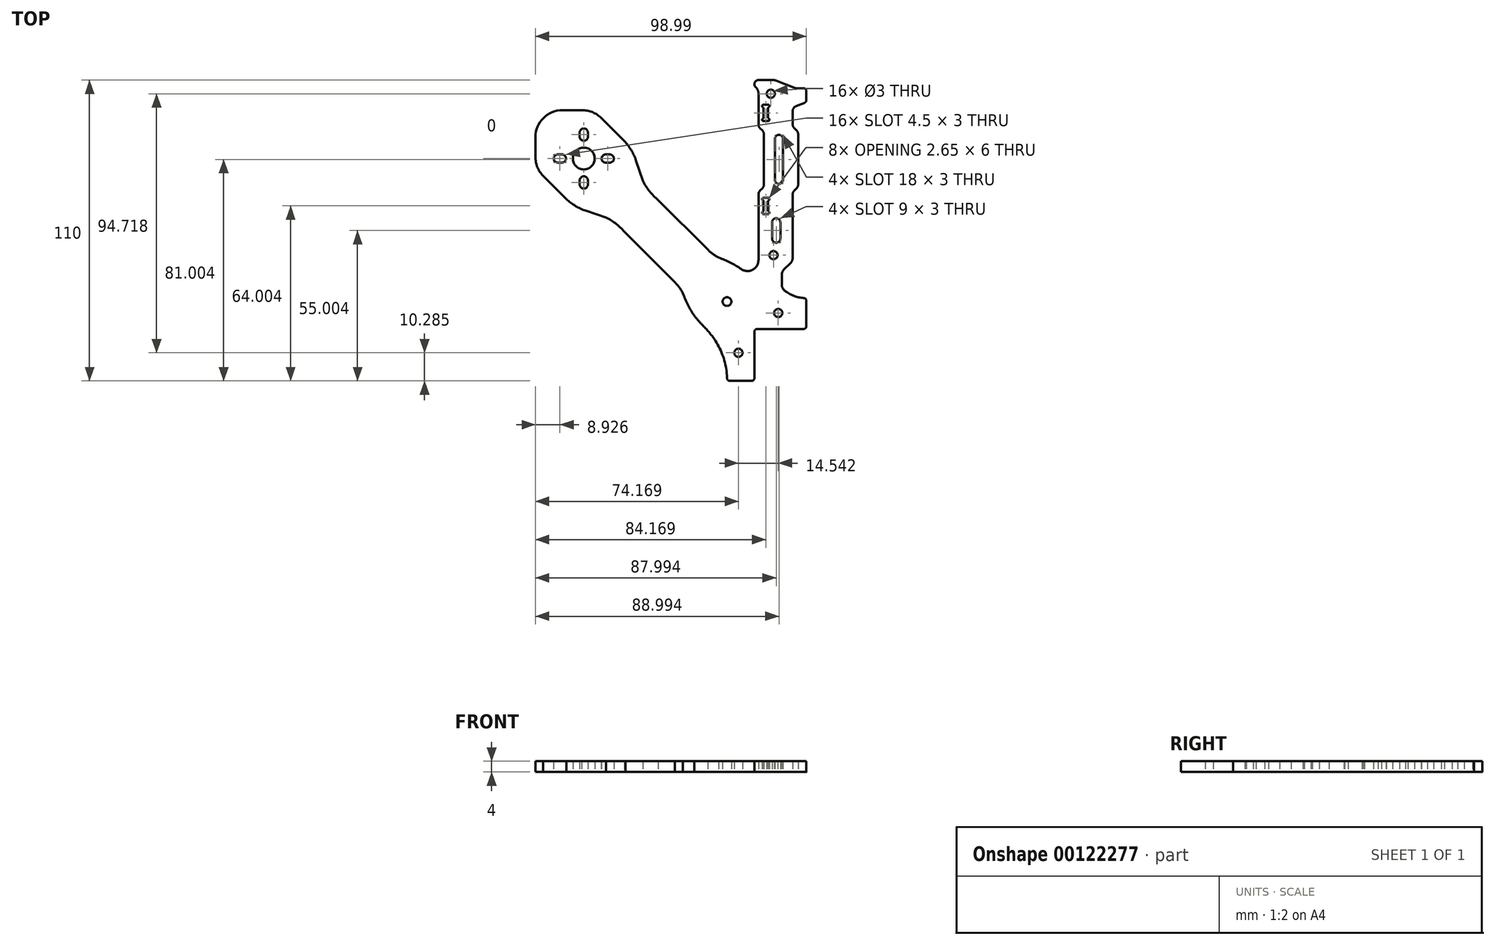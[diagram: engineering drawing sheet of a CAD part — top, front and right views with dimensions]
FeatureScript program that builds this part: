
annotation { "Feature Type Name" : "Feature", "Feature Type Description" : "" }
export const myFeature = defineFeature(function(context is Context, id is Id, definition is map)
    precondition{}
    {
        {
            var Q0;
            Q0=qCreatedBy(makeId("Top.planeOp"),FACE);
            var sketch = newSketch(context, id + "F0", { "sketchPlane" : qUnion([Q0])});
            skLineSegment(sketch, "E0", {"start": v(-69.83, -19.02) * mm, "end": v(-75.26, -19.02) * mm});
            skArc(sketch, "E1", {"start": v(-75.26, -19.02) * mm, "mid": v(-76.66, -19.98) * mm, "end": v(-76.26, -21.63) * mm});
            skLineSegment(sketch, "E2", {"start": v(-62.3, -21.8) * mm, "end": v(-68.72, -19.23) * mm});
            skArc(sketch, "E3", {"start": v(-75.26, -23.87) * mm, "mid": v(-75.52, -22.65) * mm, "end": v(-76.26, -21.63) * mm});
            skArc(sketch, "E4", {"start": v(-68.72, -19.23) * mm, "mid": v(-69.27, -19.07) * mm, "end": v(-69.83, -19.02) * mm});
            skArc(sketch, "E5", {"start": v(-62.3, -21.8) * mm, "mid": v(-61.75, -21.96) * mm, "end": v(-61.18, -22.02) * mm});
            skLineSegment(sketch, "E6", {"start": v(-61.18, -22.02) * mm, "end": v(-58.76, -22.02) * mm});
            skArc(sketch, "E7", {"start": v(-57.76, -23.02) * mm, "mid": v(-58.05, -22.3) * mm, "end": v(-58.76, -22.02) * mm});
            skLineSegment(sketch, "E8", {"start": v(-73.26, -57.19) * mm, "end": v(-73.26, -38.84) * mm});
            skLineSegment(sketch, "E9", {"start": v(-73.84, -37.43) * mm, "end": v(-74.67, -36.6) * mm});
            skLineSegment(sketch, "E10", {"start": v(-74.67, -59.43) * mm, "end": v(-73.84, -58.6) * mm});
            skLineSegment(sketch, "E11", {"start": v(-75.26, -23.87) * mm, "end": v(-75.26, -35.19) * mm});
            skArc(sketch, "E12", {"start": v(-75.26, -35.19) * mm, "mid": v(-75.1, -35.95) * mm, "end": v(-74.67, -36.6) * mm});
            skArc(sketch, "E13", {"start": v(-73.26, -38.84) * mm, "mid": v(-73.4, -38.08) * mm, "end": v(-73.84, -37.43) * mm});
            skArc(sketch, "E14", {"start": v(-74.67, -59.43) * mm, "mid": v(-75.1, -60.08) * mm, "end": v(-75.26, -60.84) * mm});
            skArc(sketch, "E15", {"start": v(-73.84, -58.6) * mm, "mid": v(-73.4, -57.95) * mm, "end": v(-73.26, -57.19) * mm});
            skCircle(sketch, "E16", {"center": v(-139.07, -47.7) * mm, "radius": 4 * mm});
            skArc(sketch, "E17", {"start": v(-148.57, -46.2) * mm, "mid": v(-150.07, -47.7) * mm, "end": v(-148.57, -49.2) * mm});
            skArc(sketch, "E18", {"start": v(-147.07, -49.2) * mm, "mid": v(-145.57, -47.7) * mm, "end": v(-147.07, -46.2) * mm});
            skArc(sketch, "E19", {"start": v(-137.57, -38.2) * mm, "mid": v(-139.07, -36.7) * mm, "end": v(-140.57, -38.2) * mm});
            skArc(sketch, "E20", {"start": v(-140.57, -39.7) * mm, "mid": v(-139.07, -41.2) * mm, "end": v(-137.57, -39.7) * mm});
            skArc(sketch, "E21", {"start": v(-131.07, -46.2) * mm, "mid": v(-132.57, -47.7) * mm, "end": v(-131.07, -49.2) * mm});
            skArc(sketch, "E22", {"start": v(-129.57, -49.2) * mm, "mid": v(-128.07, -47.7) * mm, "end": v(-129.57, -46.2) * mm});
            skArc(sketch, "E23", {"start": v(-137.57, -55.7) * mm, "mid": v(-139.07, -54.2) * mm, "end": v(-140.57, -55.7) * mm});
            skArc(sketch, "E24", {"start": v(-140.57, -57.2) * mm, "mid": v(-139.07, -58.7) * mm, "end": v(-137.57, -57.2) * mm});
            skLineSegment(sketch, "E25", {"start": v(-148.57, -46.2) * mm, "end": v(-147.07, -46.2) * mm});
            skLineSegment(sketch, "E26", {"start": v(-147.07, -49.2) * mm, "end": v(-148.57, -49.2) * mm});
            skLineSegment(sketch, "E27", {"start": v(-140.57, -38.2) * mm, "end": v(-140.57, -39.7) * mm});
            skLineSegment(sketch, "E28", {"start": v(-137.57, -38.2) * mm, "end": v(-137.57, -39.7) * mm});
            skLineSegment(sketch, "E29", {"start": v(-129.57, -46.2) * mm, "end": v(-131.07, -46.2) * mm});
            skLineSegment(sketch, "E30", {"start": v(-129.57, -49.2) * mm, "end": v(-131.07, -49.2) * mm});
            skLineSegment(sketch, "E31", {"start": v(-137.57, -55.7) * mm, "end": v(-137.57, -57.2) * mm});
            skLineSegment(sketch, "E32", {"start": v(-140.57, -55.7) * mm, "end": v(-140.57, -57.2) * mm});
            skLineSegment(sketch, "E33", {"start": v(-124.22, -41.34) * mm, "end": v(-132.7, -32.85) * mm});
            skLineSegment(sketch, "E34", {"start": v(-153.92, -54.06) * mm, "end": v(-145.44, -62.55) * mm});
            skArc(sketch, "E35", {"start": v(-146.85, -30.02) * mm, "mid": v(-153.85, -32.92) * mm, "end": v(-156.75, -39.92) * mm});
            skLineSegment(sketch, "E36", {"start": v(-146.85, -30.02) * mm, "end": v(-139.78, -30.02) * mm});
            skLineSegment(sketch, "E37", {"start": v(-156.75, -39.92) * mm, "end": v(-156.75, -47) * mm});
            skLineSegment(sketch, "E38", {"start": v(-117.5, -55.83) * mm, "end": v(-119.98, -48.4) * mm});
            skLineSegment(sketch, "E39", {"start": v(-130.94, -69.27) * mm, "end": v(-138.37, -66.8) * mm});
            skArc(sketch, "E40", {"start": v(-123.87, -74.92) * mm, "mid": v(-127.1, -71.72) * mm, "end": v(-130.94, -69.27) * mm});
            skArc(sketch, "E41", {"start": v(-117.5, -55.83) * mm, "mid": v(-115.05, -59.66) * mm, "end": v(-111.85, -62.9) * mm});
            skArc(sketch, "E42", {"start": v(-119.98, -48.4) * mm, "mid": v(-121.73, -44.65) * mm, "end": v(-124.22, -41.34) * mm});
            skArc(sketch, "E43", {"start": v(-145.44, -62.55) * mm, "mid": v(-142.12, -65.04) * mm, "end": v(-138.37, -66.8) * mm});
            skArc(sketch, "E44", {"start": v(-132.7, -32.85) * mm, "mid": v(-135.96, -30.73) * mm, "end": v(-139.78, -30.02) * mm});
            skArc(sketch, "E45", {"start": v(-156.75, -47) * mm, "mid": v(-156.04, -50.8) * mm, "end": v(-153.92, -54.06) * mm});
            skCircle(sketch, "E46", {"center": v(-69.76, -83.02) * mm, "radius": 1.5 * mm});
            skLineSegment(sketch, "E47", {"start": v(-71.76, -28.02) * mm, "end": v(-73.4, -28.02) * mm});
            skLineSegment(sketch, "E48", {"start": v(-71.76, -62.02) * mm, "end": v(-73.4, -62.02) * mm});
            skLineSegment(sketch, "E49", {"start": v(-73.4, -34.02) * mm, "end": v(-71.76, -34.02) * mm});
            skLineSegment(sketch, "E50", {"start": v(-73.4, -68.02) * mm, "end": v(-71.76, -68.02) * mm});
            skArc(sketch, "E51", {"start": v(-73.4, -28.02) * mm, "mid": v(-73.89, -28.39) * mm, "end": v(-73.66, -28.95) * mm});
            skArc(sketch, "E52", {"start": v(-73.66, -33.08) * mm, "mid": v(-73.89, -33.65) * mm, "end": v(-73.4, -34.02) * mm});
            skArc(sketch, "E53", {"start": v(-71.76, -34.02) * mm, "mid": v(-71.27, -33.65) * mm, "end": v(-71.5, -33.08) * mm});
            skArc(sketch, "E54", {"start": v(-71.5, -28.95) * mm, "mid": v(-71.27, -28.39) * mm, "end": v(-71.76, -28.02) * mm});
            skArc(sketch, "E55", {"start": v(-71.5, -62.95) * mm, "mid": v(-71.27, -62.39) * mm, "end": v(-71.76, -62.02) * mm});
            skArc(sketch, "E56", {"start": v(-73.4, -62.02) * mm, "mid": v(-73.89, -62.39) * mm, "end": v(-73.66, -62.95) * mm});
            skArc(sketch, "E57", {"start": v(-73.66, -67.08) * mm, "mid": v(-73.89, -67.65) * mm, "end": v(-73.4, -68.02) * mm});
            skArc(sketch, "E58", {"start": v(-71.76, -68.02) * mm, "mid": v(-71.27, -67.65) * mm, "end": v(-71.5, -67.08) * mm});
            skLineSegment(sketch, "E59", {"start": v(-73.4, -29.38) * mm, "end": v(-73.4, -32.65) * mm});
            skLineSegment(sketch, "E60", {"start": v(-71.76, -32.65) * mm, "end": v(-71.76, -29.38) * mm});
            skLineSegment(sketch, "E61", {"start": v(-71.76, -63.38) * mm, "end": v(-71.76, -66.65) * mm});
            skLineSegment(sketch, "E62", {"start": v(-73.4, -66.65) * mm, "end": v(-73.4, -63.38) * mm});
            skArc(sketch, "E63", {"start": v(-73.4, -29.38) * mm, "mid": v(-73.47, -29.13) * mm, "end": v(-73.66, -28.95) * mm});
            skArc(sketch, "E64", {"start": v(-71.5, -28.95) * mm, "mid": v(-71.69, -29.13) * mm, "end": v(-71.76, -29.38) * mm});
            skArc(sketch, "E65", {"start": v(-71.76, -32.65) * mm, "mid": v(-71.69, -32.9) * mm, "end": v(-71.5, -33.08) * mm});
            skArc(sketch, "E66", {"start": v(-73.66, -33.08) * mm, "mid": v(-73.47, -32.9) * mm, "end": v(-73.4, -32.65) * mm});
            skArc(sketch, "E67", {"start": v(-71.76, -66.65) * mm, "mid": v(-71.69, -66.9) * mm, "end": v(-71.5, -67.08) * mm});
            skArc(sketch, "E68", {"start": v(-73.66, -67.08) * mm, "mid": v(-73.47, -66.9) * mm, "end": v(-73.4, -66.65) * mm});
            skArc(sketch, "E69", {"start": v(-73.4, -63.38) * mm, "mid": v(-73.47, -63.13) * mm, "end": v(-73.66, -62.95) * mm});
            skArc(sketch, "E70", {"start": v(-71.5, -62.95) * mm, "mid": v(-71.69, -63.13) * mm, "end": v(-71.76, -63.38) * mm});
            skLineSegment(sketch, "E71", {"start": v(-75.26, -60.84) * mm, "end": v(-75.26, -84.84) * mm});
            skArc(sketch, "E72", {"start": v(-102.83, -97.02) * mm, "mid": v(-104.16, -94.86) * mm, "end": v(-105.84, -92.95) * mm});
            skArc(sketch, "E73", {"start": v(-93.76, -81.02) * mm, "mid": v(-91.88, -82.65) * mm, "end": v(-89.75, -83.94) * mm});
            skLineSegment(sketch, "E74", {"start": v(-60.76, -38.84) * mm, "end": v(-60.76, -57.19) * mm});
            skLineSegment(sketch, "E75", {"start": v(-62.17, -36.6) * mm, "end": v(-61.34, -37.43) * mm});
            skLineSegment(sketch, "E76", {"start": v(-61.34, -58.6) * mm, "end": v(-62.17, -59.43) * mm});
            skLineSegment(sketch, "E77", {"start": v(-62.76, -83.98) * mm, "end": v(-62.76, -60.84) * mm});
            skArc(sketch, "E78", {"start": v(-62.76, -35.19) * mm, "mid": v(-62.6, -35.95) * mm, "end": v(-62.17, -36.6) * mm});
            skArc(sketch, "E79", {"start": v(-60.76, -38.84) * mm, "mid": v(-60.9, -38.08) * mm, "end": v(-61.34, -37.43) * mm});
            skArc(sketch, "E80", {"start": v(-61.34, -58.6) * mm, "mid": v(-60.9, -57.95) * mm, "end": v(-60.76, -57.19) * mm});
            skArc(sketch, "E81", {"start": v(-62.17, -59.43) * mm, "mid": v(-62.6, -60.08) * mm, "end": v(-62.76, -60.84) * mm});
            skLineSegment(sketch, "E82", {"start": v(-62.76, -30.37) * mm, "end": v(-62.76, -35.19) * mm});
            skLineSegment(sketch, "E83", {"start": v(-66.26, -55.52) * mm, "end": v(-66.26, -40.52) * mm});
            skLineSegment(sketch, "E84", {"start": v(-69.26, -40.52) * mm, "end": v(-69.26, -55.52) * mm});
            skArc(sketch, "E85", {"start": v(-66.26, -40.52) * mm, "mid": v(-67.76, -39.02) * mm, "end": v(-69.26, -40.52) * mm});
            skArc(sketch, "E86", {"start": v(-69.26, -55.52) * mm, "mid": v(-67.76, -57.02) * mm, "end": v(-66.26, -55.52) * mm});
            skLineSegment(sketch, "E87", {"start": v(-67.26, -77.02) * mm, "end": v(-67.26, -71.02) * mm});
            skLineSegment(sketch, "E88", {"start": v(-70.26, -71.02) * mm, "end": v(-70.26, -77.02) * mm});
            skArc(sketch, "E89", {"start": v(-67.26, -71.02) * mm, "mid": v(-68.76, -69.52) * mm, "end": v(-70.26, -71.02) * mm});
            skArc(sketch, "E90", {"start": v(-70.26, -77.02) * mm, "mid": v(-68.76, -78.52) * mm, "end": v(-67.26, -77.02) * mm});
            skCircle(sketch, "E91", {"center": v(-82.58, -118.73) * mm, "radius": 1.5 * mm});
            skCircle(sketch, "E92", {"center": v(-68.04, -104.2) * mm, "radius": 1.5 * mm});
            skLineSegment(sketch, "E93", {"start": v(-58.5, -27.31) * mm, "end": v(-61.5, -28.51) * mm});
            skArc(sketch, "E94", {"start": v(-61.5, -28.51) * mm, "mid": v(-62.41, -29.25) * mm, "end": v(-62.76, -30.37) * mm});
            skLineSegment(sketch, "E95", {"start": v(-57.76, -23.02) * mm, "end": v(-57.76, -26.34) * mm});
            skArc(sketch, "E96", {"start": v(-58.42, -27.28) * mm, "mid": v(-58.46, -27.3) * mm, "end": v(-58.5, -27.31) * mm});
            skArc(sketch, "E97", {"start": v(-58.42, -27.28) * mm, "mid": v(-57.94, -26.92) * mm, "end": v(-57.76, -26.34) * mm});
            skLineSegment(sketch, "E98", {"start": v(-123.87, -74.92) * mm, "end": v(-105.84, -92.95) * mm});
            skLineSegment(sketch, "E99", {"start": v(-93.76, -81.02) * mm, "end": v(-111.85, -62.9) * mm});
            skArc(sketch, "E100", {"start": v(-75.76, -110.02) * mm, "mid": v(-76.46, -110.3) * mm, "end": v(-76.76, -111.02) * mm});
            skLineSegment(sketch, "E101", {"start": v(-75.76, -110.02) * mm, "end": v(-58.76, -110.02) * mm});
            skArc(sketch, "E102", {"start": v(-58.76, -110.02) * mm, "mid": v(-58.05, -109.72) * mm, "end": v(-57.76, -109.02) * mm});
            skLineSegment(sketch, "E103", {"start": v(-76.76, -111.02) * mm, "end": v(-76.76, -128.02) * mm});
            skArc(sketch, "E104", {"start": v(-77.76, -129.02) * mm, "mid": v(-77.05, -128.72) * mm, "end": v(-76.76, -128.02) * mm});
            skCircle(sketch, "E105", {"center": v(-70.76, -24.02) * mm, "radius": 1.5 * mm});
            skCircle(sketch, "E106", {"center": v(-86.76, -100.02) * mm, "radius": 1.6 * mm});
            skArc(sketch, "E107", {"start": v(-98.64, -105.25) * mm, "mid": v(-97.14, -107.06) * mm, "end": v(-95.52, -108.78) * mm});
            skArc(sketch, "E108", {"start": v(-90.99, -114.37) * mm, "mid": v(-93.1, -111.46) * mm, "end": v(-95.52, -108.78) * mm});
            skArc(sketch, "E109", {"start": v(-86.86, -126.19) * mm, "mid": v(-88.2, -120.03) * mm, "end": v(-90.99, -114.37) * mm});
            skArc(sketch, "E110", {"start": v(-81.52, -88.13) * mm, "mid": v(-85.5, -85.77) * mm, "end": v(-89.75, -83.94) * mm});
            skArc(sketch, "E111", {"start": v(-102.83, -97.02) * mm, "mid": v(-101, -101.27) * mm, "end": v(-98.64, -105.25) * mm});
            skArc(sketch, "E112", {"start": v(-81.52, -88.13) * mm, "mid": v(-77.4, -88.38) * mm, "end": v(-75.26, -84.84) * mm});
            skArc(sketch, "E113", {"start": v(-86.74, -128.05) * mm, "mid": v(-86.78, -127.12) * mm, "end": v(-86.86, -126.19) * mm});
            skArc(sketch, "E114", {"start": v(-86.74, -128.05) * mm, "mid": v(-86.44, -128.73) * mm, "end": v(-85.74, -129.02) * mm});
            skLineSegment(sketch, "E115", {"start": v(-85.74, -129.02) * mm, "end": v(-77.76, -129.02) * mm});
            skLineSegment(sketch, "E116", {"start": v(-66.76, -90.32) * mm, "end": v(-66.76, -93.67) * mm});
            skLineSegment(sketch, "E117", {"start": v(-63.7, -86.17) * mm, "end": v(-65.8, -88.13) * mm});
            skArc(sketch, "E118", {"start": v(-65.6, -96.04) * mm, "mid": v(-62.34, -97.89) * mm, "end": v(-58.68, -98.71) * mm});
            skArc(sketch, "E119", {"start": v(-57.76, -99.7) * mm, "mid": v(-58.02, -99.03) * mm, "end": v(-58.68, -98.71) * mm});
            skLineSegment(sketch, "E120", {"start": v(-57.76, -99.7) * mm, "end": v(-57.76, -109.02) * mm});
            skArc(sketch, "E121", {"start": v(-63.7, -86.17) * mm, "mid": v(-63, -85.18) * mm, "end": v(-62.76, -83.98) * mm});
            skArc(sketch, "E122", {"start": v(-65.8, -88.13) * mm, "mid": v(-66.5, -89.12) * mm, "end": v(-66.76, -90.32) * mm});
            skArc(sketch, "E123", {"start": v(-66.76, -93.67) * mm, "mid": v(-66.45, -94.99) * mm, "end": v(-65.6, -96.04) * mm});
            skCircle(sketch, "E124", {"center": v(-139.07, -47.7) * mm, "radius": 14 * mm, "construction": true});
            skSolve(sketch);
        }
        {
            var Q0;
            Q0 = qSketchRegion(id + "F0", true);
            extrude(context, id + "F1", {"entities" : qUnion([Q0]), "depth" : 4 * mm});
        }
    });
